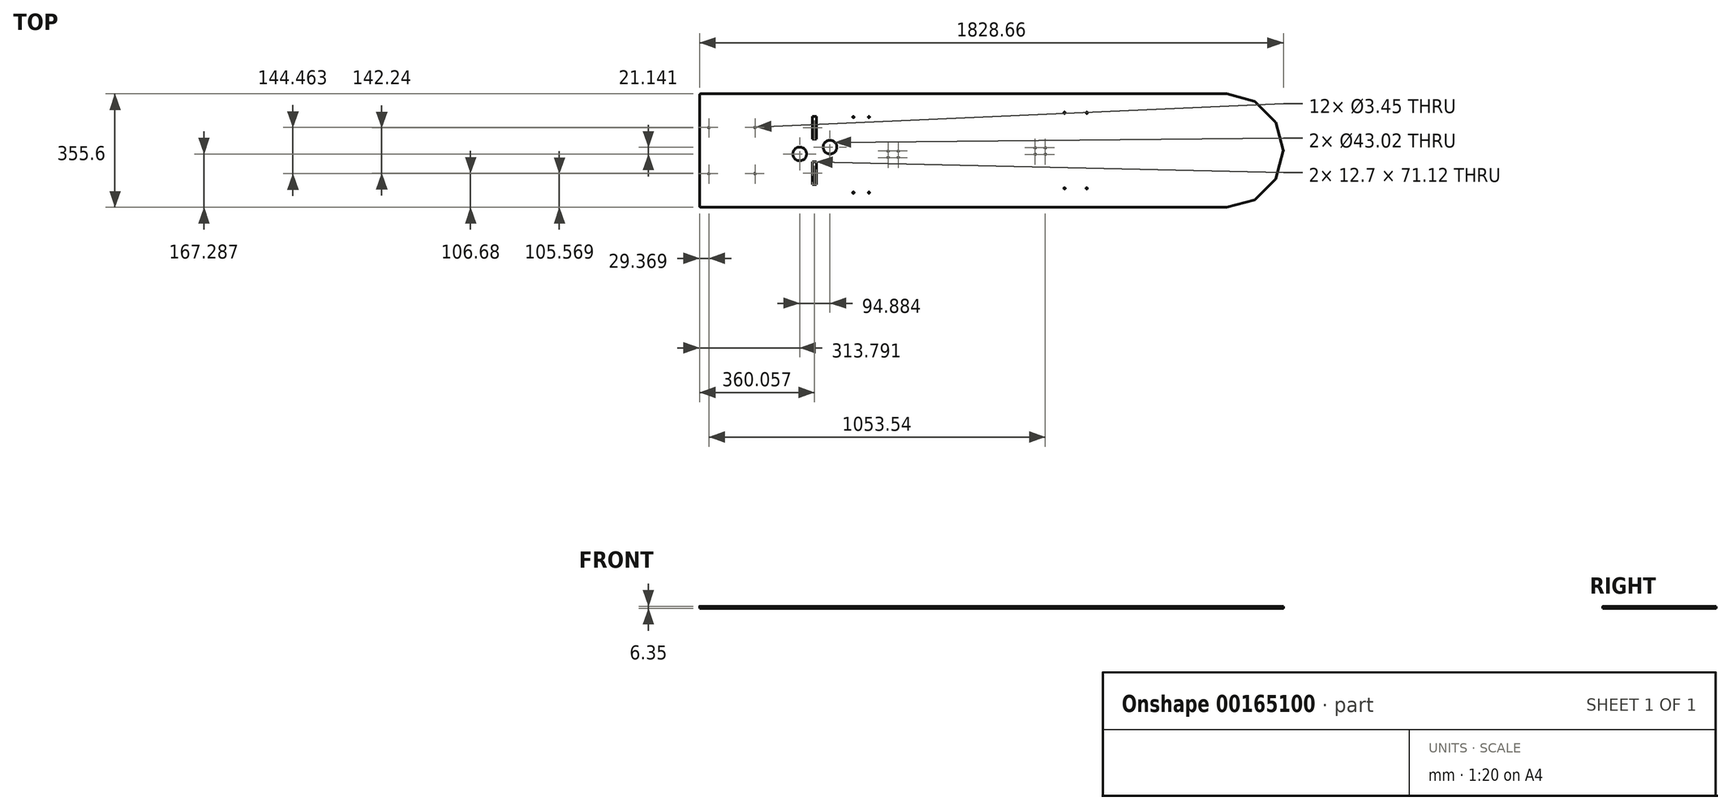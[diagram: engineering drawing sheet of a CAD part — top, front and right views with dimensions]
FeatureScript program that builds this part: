
annotation { "Feature Type Name" : "Feature", "Feature Type Description" : "" }
export const myFeature = defineFeature(function(context is Context, id is Id, definition is map)
    precondition{}
    {
        {
            var Q0;
            Q0=qCreatedBy(makeId("Top.planeOp"),FACE);
            var sketch = newSketch(context, id + "F0", { "sketchPlane" : qUnion([Q0])});
            skLineSegment(sketch, "E0", {"start": v(0, 0) * mm, "end": v(0, -177.8) * mm, "construction": true});
            skLineSegment(sketch, "E1", {"start": v(0, 0) * mm, "end": v(88.9, -153.98) * mm, "construction": true});
            skLineSegment(sketch, "E2", {"start": v(0, 0) * mm, "end": v(153.98, -88.9) * mm, "construction": true});
            skLineSegment(sketch, "E3", {"start": v(0, 0) * mm, "end": v(177.8, 0) * mm, "construction": true});
            skLineSegment(sketch, "E4", {"start": v(0, 0) * mm, "end": v(0, 177.8) * mm, "construction": true});
            skLineSegment(sketch, "E5", {"start": v(0, 0) * mm, "end": v(88.9, 153.98) * mm, "construction": true});
            skLineSegment(sketch, "E6", {"start": v(0, 0) * mm, "end": v(153.98, 88.9) * mm, "construction": true});
            skLineSegment(sketch, "E7", {"start": v(0, 177.8) * mm, "end": v(88.9, 153.98) * mm});
            skLineSegment(sketch, "E8", {"start": v(88.9, 153.98) * mm, "end": v(153.98, 88.9) * mm});
            skLineSegment(sketch, "E9", {"start": v(153.98, 88.9) * mm, "end": v(177.8, 0) * mm});
            skLineSegment(sketch, "E10", {"start": v(177.8, 0) * mm, "end": v(153.98, -88.9) * mm});
            skLineSegment(sketch, "E11", {"start": v(153.98, -88.9) * mm, "end": v(88.9, -153.98) * mm});
            skLineSegment(sketch, "E12", {"start": v(88.9, -153.98) * mm, "end": v(0, -177.8) * mm});
            skLineSegment(sketch, "E13", {"start": v(0, 177.8) * mm, "end": v(-1651, 177.8) * mm});
            skLineSegment(sketch, "E14", {"start": v(-1651, 177.8) * mm, "end": v(-1651, -177.8) * mm});
            skLineSegment(sketch, "E15", {"start": v(-1651, -177.8) * mm, "end": v(0, -177.8) * mm});
            skLineSegment(sketch, "E16", {"start": v(-304.8, 0) * mm, "end": v(-304.8, 304.8) * mm, "construction": true});
            skLineSegment(sketch, "E17.bottom", {"start": v(-457.2, 254) * mm, "end": v(-152.4, 254) * mm, "construction": true});
            skLineSegment(sketch, "E17.top", {"start": v(-457.2, 355.6) * mm, "end": v(-152.4, 355.6) * mm, "construction": true});
            skLineSegment(sketch, "E17.left", {"start": v(-457.2, 254) * mm, "end": v(-457.2, 355.6) * mm, "construction": true});
            skLineSegment(sketch, "E17.right", {"start": v(-152.4, 254) * mm, "end": v(-152.4, 355.6) * mm, "construction": true});
            skPoint(sketch, "E17.middle", {"position": v(-304.8, 304.8) * mm});
            skLineSegment(sketch, "E18", {"start": v(0, 0) * mm, "end": v(-304.8, 0) * mm, "construction": true});
            skLineSegment(sketch, "E19", {"start": v(-1651, 0) * mm, "end": v(-1549.4, 0) * mm, "construction": true});
            skLineSegment(sketch, "E20.bottom", {"start": v(-1621.63, -72.23) * mm, "end": v(-1477.17, -72.23) * mm, "construction": true});
            skLineSegment(sketch, "E20.top", {"start": v(-1621.63, 72.23) * mm, "end": v(-1477.17, 72.23) * mm, "construction": true});
            skLineSegment(sketch, "E20.left", {"start": v(-1621.63, -72.23) * mm, "end": v(-1621.63, 72.23) * mm, "construction": true});
            skLineSegment(sketch, "E20.right", {"start": v(-1477.17, -72.23) * mm, "end": v(-1477.17, 72.23) * mm, "construction": true});
            skPoint(sketch, "E20.middle", {"position": v(-1549.4, 0) * mm});
            skCircle(sketch, "E21", {"center": v(-1477.17, 72.23) * mm, "radius": 1.73 * mm});
            skCircle(sketch, "E22", {"center": v(-1621.63, 72.23) * mm, "radius": 1.73 * mm});
            skCircle(sketch, "E23", {"center": v(-1621.63, -72.23) * mm, "radius": 1.73 * mm});
            skCircle(sketch, "E24", {"center": v(-1477.17, -72.23) * mm, "radius": 1.73 * mm});
            skSolve(sketch);
        }
        {
            var Q0;
            Q0=makeQuery(id+"F0.imprint","IMPRINT",FACE,{"disambiguationData":[TD([[makeQuery(id+"F0.imprint","IMPRINT",EDGE,{"derivedFrom":sQuery(id+"F0.wireOp",EDGE,"E7")}),-1.0]])]});
            extrude(context, id + "F1", {"entities" : qUnion([Q0]), "depth" : 6.35 * mm});
        }
        {
            var Q0;
            Q0=makeQuery(id+"F1.opExtrude","CAP_FACE",FACE,{"disambiguationData":[OSD([sQuery(id+"F0.wireOp",EDGE,"E7"),sQuery(id+"F0.wireOp",EDGE,"E8"),sQuery(id+"F0.wireOp",EDGE,"E9"),sQuery(id+"F0.wireOp",EDGE,"E10"),sQuery(id+"F0.wireOp",EDGE,"E11"),sQuery(id+"F0.wireOp",EDGE,"E12"),sQuery(id+"F0.wireOp",EDGE,"E13"),sQuery(id+"F0.wireOp",EDGE,"E14"),sQuery(id+"F0.wireOp",EDGE,"E15")])],"isStart":false});
            var sketch = newSketch(context, id + "F2", { "sketchPlane" : qUnion([Q0])});
            skLineSegment(sketch, "E25", {"start": v(-583.97, -1.68) * mm, "end": v(-1044.23, -11.81) * mm, "construction": true});
            skLineSegment(sketch, "E26.bottom", {"start": v(-568.1, 8.64) * mm, "end": v(-599.84, 8.64) * mm, "construction": true});
            skLineSegment(sketch, "E26.top", {"start": v(-568.1, -12) * mm, "end": v(-599.84, -12) * mm, "construction": true});
            skLineSegment(sketch, "E26.left", {"start": v(-568.1, 8.64) * mm, "end": v(-568.1, -12) * mm, "construction": true});
            skLineSegment(sketch, "E26.right", {"start": v(-599.84, 8.64) * mm, "end": v(-599.84, -12) * mm, "construction": true});
            skPoint(sketch, "E26.middle", {"position": v(-583.97, -1.68) * mm});
            skLineSegment(sketch, "E27.bottom", {"start": v(-1028.36, -22.13) * mm, "end": v(-1060.1, -22.13) * mm, "construction": true});
            skLineSegment(sketch, "E27.top", {"start": v(-1028.36, -1.5) * mm, "end": v(-1060.1, -1.5) * mm, "construction": true});
            skLineSegment(sketch, "E27.left", {"start": v(-1028.36, -22.13) * mm, "end": v(-1028.36, -1.5) * mm, "construction": true});
            skLineSegment(sketch, "E27.right", {"start": v(-1060.1, -22.13) * mm, "end": v(-1060.1, -1.5) * mm, "construction": true});
            skPoint(sketch, "E27.middle", {"position": v(-1044.23, -11.81) * mm});
            skCircle(sketch, "E28", {"center": v(-568.1, -12) * mm, "radius": 1.73 * mm});
            skCircle(sketch, "E29", {"center": v(-599.84, -12) * mm, "radius": 1.73 * mm});
            skCircle(sketch, "E30", {"center": v(-599.84, 8.64) * mm, "radius": 1.73 * mm});
            skCircle(sketch, "E31", {"center": v(-568.1, 8.64) * mm, "radius": 1.73 * mm});
            skCircle(sketch, "E32", {"center": v(-1028.36, -1.5) * mm, "radius": 1.73 * mm});
            skCircle(sketch, "E33", {"center": v(-1028.36, -22.13) * mm, "radius": 1.73 * mm});
            skCircle(sketch, "E34", {"center": v(-1060.1, -22.13) * mm, "radius": 1.73 * mm});
            skCircle(sketch, "E35", {"center": v(-1060.1, -1.5) * mm, "radius": 1.73 * mm});
            skLineSegment(sketch, "E36.bottom", {"start": v(-507.79, -118.37) * mm, "end": v(-438.05, -118.37) * mm, "construction": true});
            skLineSegment(sketch, "E36.top", {"start": v(-507.79, 118.37) * mm, "end": v(-438.05, 118.37) * mm, "construction": true});
            skLineSegment(sketch, "E36.left", {"start": v(-507.79, -118.37) * mm, "end": v(-507.79, 118.37) * mm, "construction": true});
            skLineSegment(sketch, "E36.right", {"start": v(-438.05, -118.37) * mm, "end": v(-438.05, 118.37) * mm, "construction": true});
            skPoint(sketch, "E36.middle", {"position": v(-472.92, 0) * mm});
            skCircle(sketch, "E37", {"center": v(-438.05, 118.37) * mm, "radius": 2.15 * mm});
            skCircle(sketch, "E38", {"center": v(-507.79, 118.37) * mm, "radius": 2.15 * mm});
            skCircle(sketch, "E39", {"center": v(-507.79, -118.37) * mm, "radius": 2.15 * mm});
            skCircle(sketch, "E40", {"center": v(-438.05, -118.37) * mm, "radius": 2.15 * mm});
            skLineSegment(sketch, "E41.bottom", {"start": v(-1120.41, -131.86) * mm, "end": v(-1169.15, -131.86) * mm, "construction": true});
            skLineSegment(sketch, "E41.top", {"start": v(-1120.41, 104.88) * mm, "end": v(-1169.15, 104.88) * mm, "construction": true});
            skLineSegment(sketch, "E41.left", {"start": v(-1120.41, -131.86) * mm, "end": v(-1120.41, 104.88) * mm, "construction": true});
            skLineSegment(sketch, "E41.right", {"start": v(-1169.15, -131.86) * mm, "end": v(-1169.15, 104.88) * mm, "construction": true});
            skPoint(sketch, "E41.middle", {"position": v(-1144.78, -13.49) * mm});
            skCircle(sketch, "E42", {"center": v(-1169.15, -131.86) * mm, "radius": 2.15 * mm});
            skCircle(sketch, "E43", {"center": v(-1120.41, -131.86) * mm, "radius": 2.15 * mm});
            skCircle(sketch, "E44", {"center": v(-1169.15, 104.88) * mm, "radius": 2.15 * mm});
            skCircle(sketch, "E45", {"center": v(-1120.41, 104.88) * mm, "radius": 2.15 * mm});
            skLineSegment(sketch, "E46", {"start": v(-1120.41, -13.49) * mm, "end": v(-1044.23, -11.81) * mm, "construction": true});
            skLineSegment(sketch, "E47", {"start": v(-507.79, 0) * mm, "end": v(-583.97, -1.68) * mm, "construction": true});
            skLineSegment(sketch, "E48", {"start": v(-1169.15, -13.49) * mm, "end": v(-1242.33, -13.49) * mm, "construction": true});
            skLineSegment(sketch, "E49.bottom", {"start": v(-1284.6, 106.68) * mm, "end": v(-1297.3, 106.68) * mm});
            skLineSegment(sketch, "E49.top", {"start": v(-1284.6, 35.56) * mm, "end": v(-1297.3, 35.56) * mm});
            skLineSegment(sketch, "E49.left", {"start": v(-1284.6, 106.68) * mm, "end": v(-1284.6, 35.56) * mm});
            skLineSegment(sketch, "E49.right", {"start": v(-1297.3, 106.68) * mm, "end": v(-1297.3, 35.56) * mm});
            skLineSegment(sketch, "E50.bottom", {"start": v(-1284.6, -35.56) * mm, "end": v(-1297.3, -35.56) * mm});
            skLineSegment(sketch, "E50.top", {"start": v(-1284.6, -106.68) * mm, "end": v(-1297.3, -106.68) * mm});
            skLineSegment(sketch, "E50.left", {"start": v(-1284.6, -35.56) * mm, "end": v(-1284.6, -106.68) * mm});
            skLineSegment(sketch, "E50.right", {"start": v(-1297.3, -35.56) * mm, "end": v(-1297.3, -106.68) * mm});
            skLineSegment(sketch, "E51", {"start": v(-1290.94, 177.8) * mm, "end": v(-1290.94, 106.68) * mm, "construction": true});
            skLineSegment(sketch, "E52", {"start": v(-1290.94, 35.56) * mm, "end": v(-1290.94, -35.56) * mm, "construction": true});
            skLineSegment(sketch, "E53", {"start": v(-1290.94, -106.68) * mm, "end": v(-1290.94, -177.8) * mm, "construction": true});
            skLineSegment(sketch, "E54", {"start": v(-1290.94, 0) * mm, "end": v(-1242.33, -13.49) * mm, "construction": true});
            skLineSegment(sketch, "E55", {"start": v(-1242.33, -13.49) * mm, "end": v(-1242.33, 10.63) * mm, "construction": true});
            skLineSegment(sketch, "E56", {"start": v(-1290.94, 0) * mm, "end": v(-1339.56, 13.49) * mm, "construction": true});
            skLineSegment(sketch, "E57", {"start": v(-1337.2, -10.51) * mm, "end": v(-1339.56, 13.49) * mm, "construction": true});
            skCircle(sketch, "E58", {"center": v(-1337.2, -10.51) * mm, "radius": 21.51 * mm});
            skCircle(sketch, "E59", {"center": v(-1242.33, 10.63) * mm, "radius": 21.51 * mm});
            skLineSegment(sketch, "E60", {"start": v(-1477.17, 72.23) * mm, "end": v(-1477.17, -72.23) * mm, "construction": true});
            skLineSegment(sketch, "E61", {"start": v(-1477.17, 0) * mm, "end": v(-1339.56, 13.49) * mm, "construction": true});
            skSolve(sketch);
        }
        {
            var Q0;
            Q0=qSketchRegion(id+"F2",true);
            var Q1;
            Q1=makeQuery(id+"F1.opExtrude","CAP_FACE",FACE,{"disambiguationData":[OSD([sQuery(id+"F0.wireOp",EDGE,"E7"),sQuery(id+"F0.wireOp",EDGE,"E8"),sQuery(id+"F0.wireOp",EDGE,"E9"),sQuery(id+"F0.wireOp",EDGE,"E10"),sQuery(id+"F0.wireOp",EDGE,"E11"),sQuery(id+"F0.wireOp",EDGE,"E12"),sQuery(id+"F0.wireOp",EDGE,"E13"),sQuery(id+"F0.wireOp",EDGE,"E14"),sQuery(id+"F0.wireOp",EDGE,"E15")])],"isStart":true});
            extrude(context, id + "F3", {"entities" : qUnion([Q0]), "operationType" : NewBodyOperationType.REMOVE, "endBound" : BoundingType.UP_TO_SURFACE, "oppositeDirection" : true, "endBoundEntityFace" : qUnion([Q1]), "depth" : 25.4 * mm});
        }
        {
            var Q0;
            Q0=makeQuery(id+"F1.opExtrude","SWEPT_EDGE",EDGE,{"disambiguationData":[OSD([sQuery(id+"F0.wireOp",EDGE,"E12"),sQuery(id+"F0.wireOp",EDGE,"E15")])]});
            var Q1;
            Q1=makeQuery(id+"F1.opExtrude","SWEPT_EDGE",EDGE,{"disambiguationData":[OSD([sQuery(id+"F0.wireOp",EDGE,"E11"),sQuery(id+"F0.wireOp",EDGE,"E12")])]});
            var Q2;
            Q2=makeQuery(id+"F1.opExtrude","SWEPT_EDGE",EDGE,{"disambiguationData":[OSD([sQuery(id+"F0.wireOp",EDGE,"E10"),sQuery(id+"F0.wireOp",EDGE,"E11")])]});
            var Q3;
            Q3=makeQuery(id+"F1.opExtrude","SWEPT_EDGE",EDGE,{"disambiguationData":[OSD([sQuery(id+"F0.wireOp",EDGE,"E9"),sQuery(id+"F0.wireOp",EDGE,"E10")])]});
            var Q4;
            Q4=makeQuery(id+"F1.opExtrude","SWEPT_EDGE",EDGE,{"disambiguationData":[OSD([sQuery(id+"F0.wireOp",EDGE,"E8"),sQuery(id+"F0.wireOp",EDGE,"E9")])]});
            var Q5;
            Q5=makeQuery(id+"F1.opExtrude","SWEPT_EDGE",EDGE,{"disambiguationData":[OSD([sQuery(id+"F0.wireOp",EDGE,"E7"),sQuery(id+"F0.wireOp",EDGE,"E8")])]});
            var Q6;
            Q6=makeQuery(id+"F1.opExtrude","SWEPT_EDGE",EDGE,{"disambiguationData":[OSD([sQuery(id+"F0.wireOp",EDGE,"E7"),sQuery(id+"F0.wireOp",EDGE,"E13")])]});
            var Q7;
            Q7=makeQuery(id+"F1.opExtrude","SWEPT_EDGE",EDGE,{"disambiguationData":[OSD([sQuery(id+"F0.wireOp",EDGE,"E13"),sQuery(id+"F0.wireOp",EDGE,"E14")])]});
            var Q8;
            Q8=makeQuery(id+"F1.opExtrude","SWEPT_EDGE",EDGE,{"disambiguationData":[OSD([sQuery(id+"F0.wireOp",EDGE,"E14"),sQuery(id+"F0.wireOp",EDGE,"E15")])]});
            fillet(context, id + "F4", {"entities" : qUnion([Q0, Q1, Q2, Q3, Q4, Q5, Q6, Q7, Q8]), "radius" : 3.97 * mm, "tangentPropagation" : true, "allowEdgeOverflow" : false});
        }
    });
